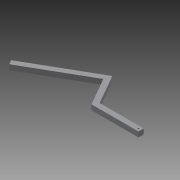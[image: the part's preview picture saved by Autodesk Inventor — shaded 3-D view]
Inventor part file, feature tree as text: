
AUTODESK INVENTOR PART (.ipt)
format: ipt  version: 2013 (Build 170138000, 138)  size: 95,232 bytes
history: native  units: in
note: dims shown in document units (in); Inventor stores cm internally (conversion verified against a paired STEP export)
features: extrude x3, sketch x3
ambient origin geometry x8: Origin, YZ Plane, XZ Plane, XY Plane, X Axis, Y Axis, Z Axis, Center Point
bodies: Solid1 (feature_tree)
feature tree (6):
  extrude  "Extrusion1"  Depth=1.0in
  extrude  "Extrusion2"  Depth=0.5in
  extrude  "Extrusion3"  Depth=1.0in TaperAngle=0.0deg
  sketch  "Sketch1"  dims[d0=1.0in d1=1.0in d2=1.0in d3=1.0in d4=1.0in d5=1.0in]
  sketch  "Sketch2"  dims[d6=1.0in d7=0.0in d8=0.5in]
  sketch  "Sketch3"  dims[d9=0.266in d10=1.0in d11=0.0in d12=2.5in d13=0.0in]
